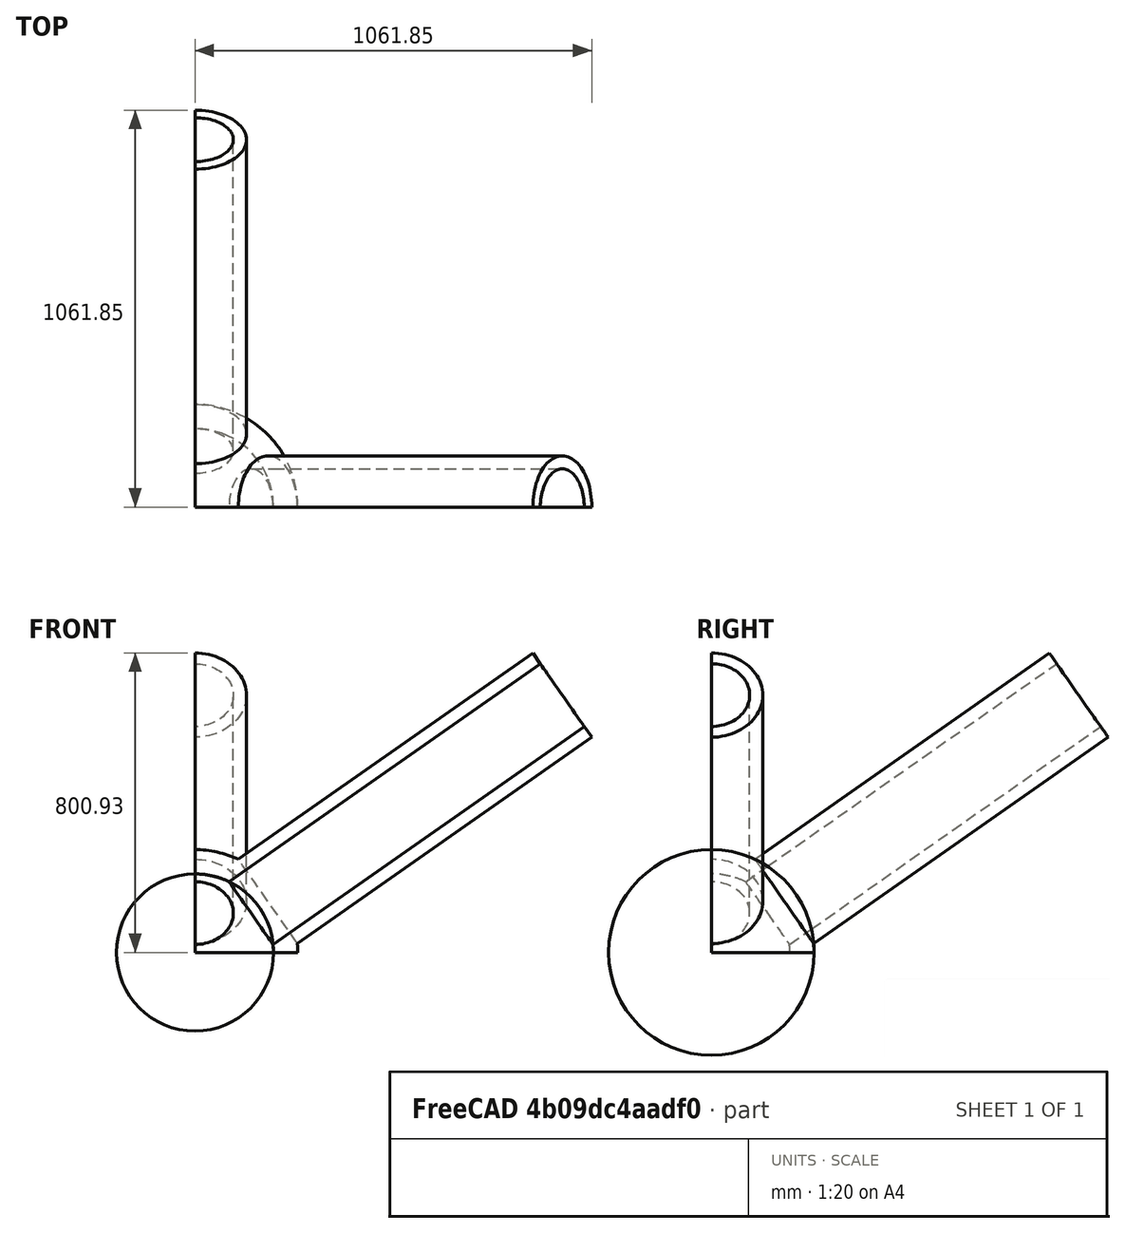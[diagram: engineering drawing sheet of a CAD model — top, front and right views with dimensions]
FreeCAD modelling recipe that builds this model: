
FCSTD DOCUMENT  (FreeCAD 0.16RUnknown)
Label: Basic Header Tutorial
License: All rights reserved
LicenseURL: http://en.wikipedia.org/wiki/All_rights_reserved
objects: Part::Thickness×3, Fem::ConstraintDisplacement×3, Part::Cylinder×2, Part::FeaturePython×2, Part::Box×2, Part::Cut×2, Fem::ConstraintForce×2, Part::Sphere×1, Fem::FemSolverObjectPython×1, Fem::FemMeshShapeNetgenObject×1, App::MaterialObjectPython×1, Fem::ConstraintPressure×1, Fem::FemResultObject×1, Fem::FemAnalysisPython×1, Fem::FemPostPipeline×1
note: 12 computed .brp shape members not serialized (recipe doc carries the construction recipe); baked Part::Feature solids carry a one-line shape summary decoded from their .brp

FEATURE [Part::Sphere] Sphere
  Angle1 = -90
  Angle2 = 90
  Angle3 = 180
  Placement = pos=(0,0,0) rot=(1,0,0;1.5708rad)
  Radius = 210
FEATURE [Part::Cylinder] Cylinder
  Angle = 360
  Height = 1200
  Radius = 102.5
FEATURE [Part::Thickness] Thickness
  Faces = -> Sphere [Face2,Face3]
  Intersection = false
  Join = 0
  Mode = 0
  SelfIntersection = false
  Value = 65
FEATURE [Part::Thickness] Thickness001
  Faces = -> Cylinder [Face3,Face2]
  Intersection = false
  Join = 0
  Mode = 0
  Placement = pos=(0,0,0) rot=(0,1,0;0.959931rad)
  SelfIntersection = false
  Value = 35
FEATURE [Part::Cylinder] Cylinder001
  Angle = 360
  Height = 1200
  Radius = 102.5
FEATURE [Part::Thickness] Thickness002
  Faces = -> Cylinder001 [Face2,Face3]
  Intersection = false
  Join = 0
  Mode = 0
  Placement = pos=(0,0,0) rot=(-1,0,0;0.959931rad)
  SelfIntersection = false
  Value = 35
FEATURE [Part::FeaturePython] Connect  # WARN: FeaturePython — macro-defined, semantics opaque (R4)
  Base = -> Thickness
  Mode = 1
  Tool = -> Thickness001
FEATURE [Part::FeaturePython] Connect001  # WARN: FeaturePython — macro-defined, semantics opaque (R4)
  Base = -> Connect
  Mode = 1
  Tool = -> Thickness002
FEATURE [Part::Box] Box  label="Cube"
  Height = 1000
  Length = 1500
  Placement = pos=(-300,-500,0) rot=(0,0,1;0rad)
  Width = 500
FEATURE [Part::Cut] Cut
  Base = -> Connect001
  Tool = -> Box
FEATURE [Part::Box] Box001  label="Cube001"
  Height = 1000
  Length = 500
  Placement = pos=(-500,0,0) rot=(0,0,1;0rad)
  Width = 1500
FEATURE [Part::Cut] Cut001  label="Header"
  Base = -> Cut
  Tool = -> Box001
FEATURE [Fem::FemSolverObjectPython] CalculiX  # FEM object (typed FeaturePython)
  AnalysisType = 0
  EigenmodeHighLimit = 1000000
  EigenmodeLowLimit = 0
  EndTime = 1
  InitialTimeStep = 0.01
  MatrixSolverType = 0
  Maxiterations = 2000
  NonLinearGeometry = false
  NumCpus = 3
  NumberOfEigenmodes = 10
  SolverType = FemSolverCalculix
  SteadyState = true
FEATURE [Fem::FemMeshShapeNetgenObject] Cut001_Mesh
  Fineness = 0
  GrowthRate = 0.3
  MaxSize = 1000
  NbSegsPerEdge = 1
  NbSegsPerRadius = 2
  Optimize = true
  SecondOrder = true
  Shape = -> Cut001
FEATURE [App::MaterialObjectPython] MechanicalMaterial  # material (typed FeaturePython)
  Material = Density=7900.0 kg/m^3,Description=Standard steel material for CalculiX sample calculations,Father=Metal,Name=CalculiX-Steel,PoissonRatio=0.3,+4 more (map truncated)
FEATURE [Fem::ConstraintDisplacement] FemConstraintDisplacement
  NormalDirection = (0,-1,0)
  Normals = (3) [(0,-1,0),(0,-1,0),(0,-1,0)]
  Points = (3) [(616.127,0,596.981),(493.237,0,201.443),(777.543,0,402.886)]
  References = -> [Cut001]
  Scale = 29
  rotxFix = false
  rotxFree = true
  rotyFix = false
  rotyFree = true
  rotzFix = false
  rotzFree = true
  xDisplacement = 0
  xFix = false
  xFree = true
  xRotation = 0
  yDisplacement = 0
  yFix = true
  yFree = false
  yRotation = 0
  zDisplacement = 0
  zFix = false
  zFree = true
  zRotation = 0
FEATURE [Fem::ConstraintDisplacement] FemConstraintDisplacement001
  NormalDirection = (-1,0,0)
  Normals = (3) [(-1,0,0),(-1,0,0),(-1,0,0)]
  Points = (3) [(0,616.127,596.981),(0,777.543,402.886),(0,493.237,201.443)]
  References = -> [Cut001]
  Scale = 29
  rotxFix = false
  rotxFree = true
  rotyFix = false
  rotyFree = true
  rotzFix = false
  rotzFree = true
  xDisplacement = 0
  xFix = true
  xFree = false
  xRotation = 0
  yDisplacement = 0
  yFix = false
  yFree = true
  yRotation = 0
  zDisplacement = 0
  zFix = false
  zFree = true
  zRotation = 0
FEATURE [Fem::ConstraintDisplacement] FemConstraintDisplacement002
  NormalDirection = (0,0,-1)
  Normals = (15) [(0,2.22045e-16,-1),(0,2.22045e-16,-1),(0,2.22045e-16,-1),(0,2.22045e-16,-1),(0,2.22045e-16,-1),(0,2.22045e-16,-1),(0,2.22045e-16,-1),+8 more]
  Points = (15) [(-3.36778e-14,275,6.10623e-14),(183.333,183.333,4.07082e-14),(275,0,0),(-3.85764e-14,239.724,5.32294e-14),(-3.85764e-14,224.405,4.9828e-14),+10 more]
  References = -> [Cut001]
  Scale = 7
  rotxFix = false
  rotxFree = true
  rotyFix = false
  rotyFree = true
  rotzFix = false
  rotzFree = true
  xDisplacement = 0
  xFix = false
  xFree = true
  xRotation = 0
  yDisplacement = 0
  yFix = false
  yFree = true
  yRotation = 0
  zDisplacement = 0
  zFix = true
  zFree = false
  zRotation = 0
FEATURE [Fem::ConstraintPressure] FemConstraintPressure
  NormalDirection = (-0.707107,0.40558,-0.579228)
  Normals = (104) [(1.83697e-16,0.573576,-0.819152),(-0.5,0.496732,-0.709406),(-0.866025,0.286788,-0.409576),(-1,1.40486e-16,-2.00634e-16),+100 more]
  Points = (104) [(-1.88289e-14,150.243,230.33),(51.25,158.119,219.082),(88.7676,179.639,188.349),(102.5,209.034,146.367),(-1.88289e-14,343.73,365.812),+99 more]
  Pressure = 17.1
  References = -> [Cut001]
  Scale = 27
FEATURE [Fem::ConstraintForce] FemConstraintForce
  DirectionVector = (0,0.819152,0.573576)
  Force = 386604
  NormalDirection = (0,0.819152,0.573576)
  Points = (2) [(-2.52583e-14,904.116,800.925),(-2.52583e-14,1061.85,575.658)]
  References = -> [Cut001]
  Scale = 15
FEATURE [Fem::ConstraintForce] FemConstraintForce001
  DirectionVector = (0.819152,0,0.573576)
  Force = 386604
  NormalDirection = (0.819152,0,0.573576)
  Points = (2) [(904.116,0,800.925),(1061.85,0,575.658)]
  References = -> [Cut001]
  Scale = 15
FEATURE [Fem::FemResultObject] Results
  DisplacementLengths = [0.128779,0.066209,0.0788357,0.127362,0.0779502,0.0680642,0.129427,0.127583,0.0738405,0.127917,0.12984,0.0712244,0.0682648,0.127146,0.128073,0.062857,0.0772628,0.0771443,0.0662338,0.0689709,0.0701065,0.0613024,0.0702129,0.0630654,0.128429,+7239 more]
  DisplacementVectors = (7264) [(0.0277188,0.0992332,0.0772562),(0.0442675,0.042758,0.0244086),(0.0539749,0.0504928,0.0274273),(0.0224917,0.098881,0.0770576),(0,0.0118127,0.0770499),+7259 more]
  Eigenmode = 0
  EigenmodeFrequency = 0
  MaxShear = [35.38,53.646,63.8111,20.5027,50.3746,44.7999,36.7707,21.7229,41.592,21.8929,37.3582,39.4397,43.9699,21.6793,37.1472,54.796,74.9136,67.9777,39.9345,39.7728,34.2484,13.1056,34.0522,56.1044,36.715,21.8865,40.7217,42.805,47.0074,43.8634,+7234 more]
  Mesh = -> Cut001_Mesh
  NodeNumbers = [1,2,3,4,5,6,7,8,9,10,11,12,13,14,15,16,17,18,19,20,21,22,23,24,25,26,27,28,29,30,31,32,33,34,35,36,37,38,39,40,41,42,43,44,45,46,47,48,49,50,51,52,53,54,55,56,57,58,59,60,61,62,63,64,65,66,67,68,69,+7195 more]
  PrincipalMax = [52.6676,79.4639,86.2754,39.8946,79.0073,75.6035,66.0315,48.2754,68.0808,48.5934,66.7644,65.108,75.0472,48.0726,66.8853,107.639,134.464,118.638,95.5693,88.2163,77.747,26.4663,74.852,108.845,66.1053,48.2335,95.1927,71.0489,76.8203,71.0197,+7234 more]
  PrincipalMed = [39.9342,34.3082,17.1373,33.7308,-13.0797,6.88944,15.8021,19.2896,36.5683,19.2744,15.6425,63.7593,7.02267,19.8374,15.4147,4.84189,-14.359,-3.02874,36.9317,46.8633,60.9222,26.1584,52.3166,4.24067,15.3542,19.7945,38.3864,30.2932,21.3919,+7235 more]
  PrincipalMin = [-18.0923,-27.8282,-41.3468,-1.11081,-21.7419,-13.9964,-7.50988,4.82949,-15.1032,4.80758,-7.95193,-13.7714,-12.8926,4.71395,-7.40918,-1.95296,-15.3629,-17.3173,15.7004,8.67066,9.25015,0.255033,6.74752,-3.36367,-7.32473,4.46047,13.7493,+7237 more]
  Stats = [0,0.0393608,0.116031,0,0.044267,0.115645,-0.00613744,0.0476984,0.0998939,0.0595291,0.0875723,0.12984,26.0587,67.2917,149.42,26.4663,66.0288,134.998,-16.6381,22.4671,70.9724,-42.4832,-8.90169,16.6106,13.1056,37.4652,77.7047]
  StressValues = [65.3306,93.3048,110.652,38.2974,96.7095,81.1972,65.0952,38.3198,72.7412,38.64,66.1539,78.2138,79.8667,38.1177,65.9159,106.358,149.328,129.404,71.6526,68.9067,61.826,26.0587,60.0941,108.606,65.1229,38.4707,72.3428,74.1688,81.8535,76.0556,+7234 more]
  Temperature = [0]
  Time = 0
FEATURE [Fem::FemAnalysisPython] MechanicalAnalysis  # FEM object (typed FeaturePython)
  Member = -> [CalculiX,Cut001_Mesh,MechanicalMaterial,FemConstraintDisplacement,FemConstraintDisplacement001,FemConstraintDisplacement002,FemConstraintPressure,FemConstraintForce,FemConstraintForce001,Results]
FEATURE [Fem::FemPostPipeline] Pipeline
  Mode = 0
